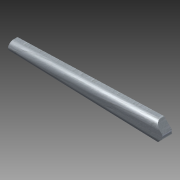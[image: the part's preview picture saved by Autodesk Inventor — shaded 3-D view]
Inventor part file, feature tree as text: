
AUTODESK INVENTOR PART (.ipt)
format: ipt  version: 2011 SP1 (Build 150282100, 282)  size: 95,232 bytes
history: native  units: in
note: dims shown in document units (in); Inventor stores cm internally (conversion verified against a paired STEP export)
features: extrude x1, fillet x1, hole x1, sketch x1
ambient origin geometry x8: Origin, YZ Plane, XZ Plane, XY Plane, X Axis, Y Axis, Z Axis, Center Point
bodies: Solid1 (feature_tree)
feature tree (4):
  extrude  "Extrusion1"  Depth=0.25in
  fillet  "Fillet2"  Radius=0.25in
  hole  "Hole1"  [1 undecoded]
  sketch  "Sketch1"  dims[d1=0.25in d3=0.25in d4=0.25in d5=0.0in d8=0.15in d10=135.0deg d11=4.0625in d12=0.0in d13=0.0in d14=0.125in d15=0.75in d16=0.375in d17=0.25in d18=0.5635in d19=1.0in d20=0.8108in]
note: 1 required parameter value undecoded (feature->parameter linkage not recoverable at this tier; creation-order binding heuristic only, values carry confidence <= 0.55)
